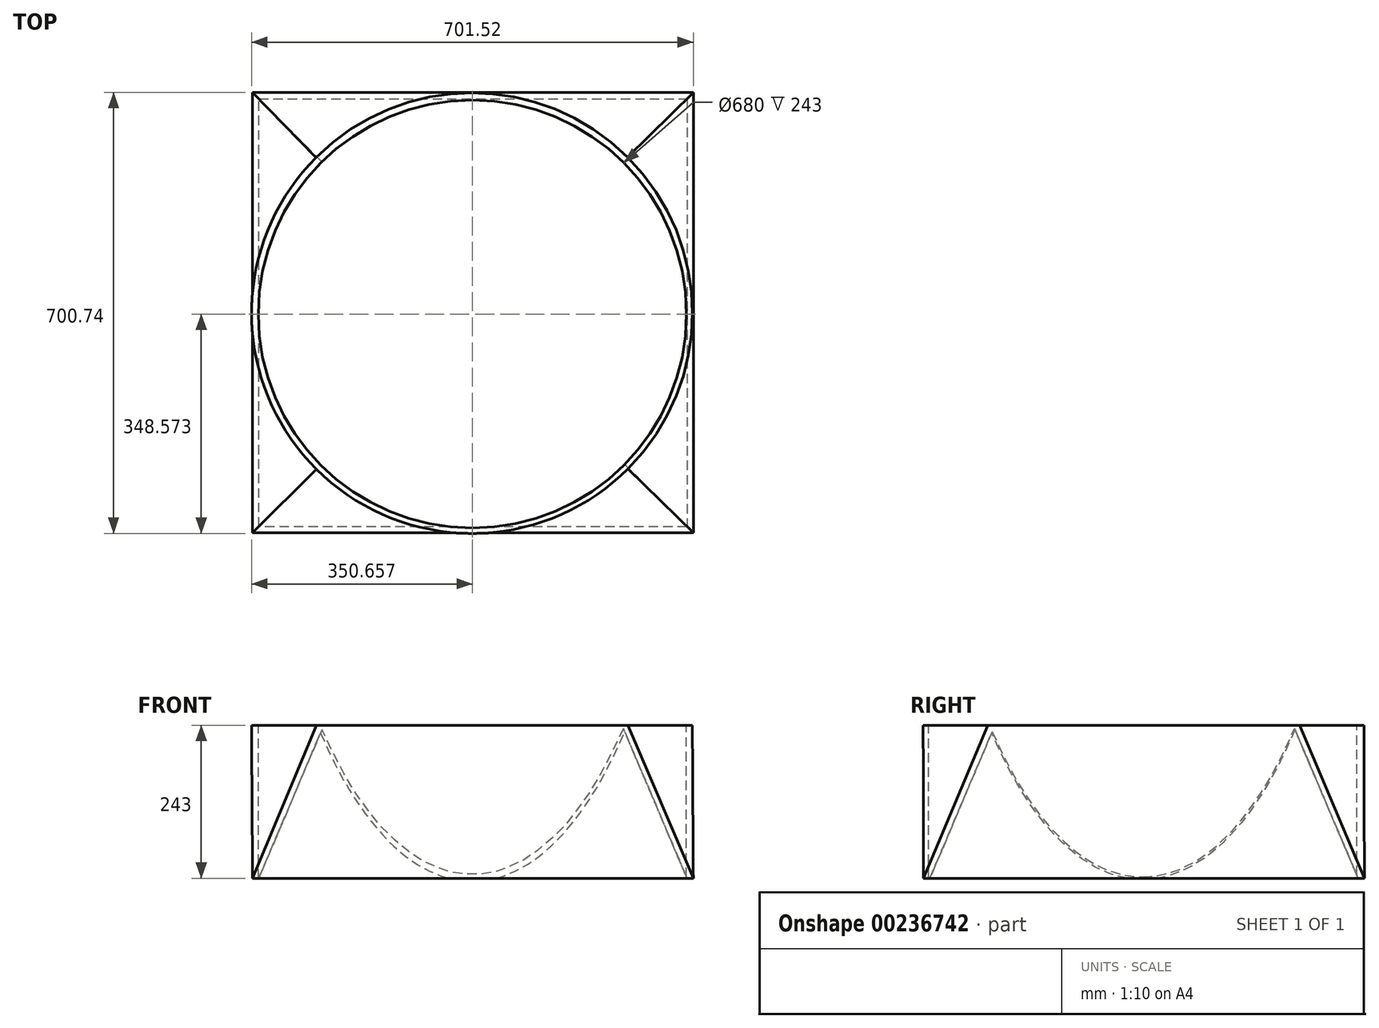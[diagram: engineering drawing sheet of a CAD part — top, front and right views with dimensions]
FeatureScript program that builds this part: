
annotation { "Feature Type Name" : "Feature", "Feature Type Description" : "" }
export const myFeature = defineFeature(function(context is Context, id is Id, definition is map)
    precondition{}
    {
        {
            var Q0;
            Q0=qCreatedBy(makeId("Top.planeOp"),FACE);
            var sketch = newSketch(context, id + "F0", { "sketchPlane" : qUnion([Q0])});
            skLineSegment(sketch, "E0.bottom", {"start": v(0, 0) * mm, "end": v(700, 0) * mm});
            skLineSegment(sketch, "E0.top", {"start": v(0, 700) * mm, "end": v(700, 700) * mm});
            skLineSegment(sketch, "E0.left", {"start": v(0, 0) * mm, "end": v(0, 700) * mm});
            skLineSegment(sketch, "E0.right", {"start": v(700, 0) * mm, "end": v(700, 700) * mm});
            skSolve(sketch);
        }
        {
            var Q0;
            Q0=makeQuery(id+"F0.imprint","IMPRINT",FACE,{"disambiguationData":[TD([[makeQuery(id+"F0.imprint","IMPRINT",EDGE,{"derivedFrom":sQuery(id+"F0.wireOp",EDGE,"E0.bottom")}),1.0]])]});
            cPlane(context, id + "F1", {"entities" : qUnion([Q0]), "cplaneType" : CPlaneType.OFFSET, "offset" : 243 * mm, "width" : 150 * mm, "height" : 150 * mm});
        }
        {
            var Q0;
            Q0=qCreatedBy(id+"F1.planeOp",FACE);
            var sketch = newSketch(context, id + "F2", { "sketchPlane" : qUnion([Q0])});
            skCircle(sketch, "E1", {"center": v(348.48, 349.26) * mm, "radius": 350 * mm});
            skLineSegment(sketch, "E2", {"start": v(0, 0) * mm, "end": v(696.95, 698.51) * mm, "construction": true});
            skLineSegment(sketch, "E3", {"start": v(0, 698.34) * mm, "end": v(698.47, 0) * mm, "construction": true});
            skSolve(sketch);
        }
        {
            var Q0;
            Q0=makeQuery(id+"F2.imprint","IMPRINT",FACE,{"disambiguationData":[TD([[makeQuery(id+"F2.imprint","IMPRINT",EDGE,{"derivedFrom":sQuery(id+"F2.wireOp",EDGE,"E1")}),1.0]])]});
            var Q1;
            Q1=makeQuery(id+"F0.imprint","IMPRINT",FACE,{"disambiguationData":[TD([[makeQuery(id+"F0.imprint","IMPRINT",EDGE,{"derivedFrom":sQuery(id+"F0.wireOp",EDGE,"E0.bottom")}),1.0]])]});
            loft(context, id + "F3", {"sheetProfilesArray" : [{ "sheetProfileEntities" : qUnion([Q0]) }, { "sheetProfileEntities" : qUnion([Q1]) }]});
        }
        {
            var Q0;
            Q0=makeQuery(id+"F3.opLoft","CAP_FACE",FACE,{"disambiguationData":[OSD([makeQuery(id+"F2.imprint","IMPRINT",FACE,{"disambiguationData":[TD([[makeQuery(id+"F2.imprint","IMPRINT",EDGE,{"derivedFrom":sQuery(id+"F2.wireOp",EDGE,"E1")}),1.0]])]})])],"isStart":true});
            var sketch = newSketch(context, id + "F4", { "sketchPlane" : qUnion([Q0])});
            skCircle(sketch, "E4", {"center": v(349.14, 347.83) * mm, "radius": 340 * mm});
            skSolve(sketch);
        }
        {
            var Q0;
            Q0=makeQuery(id+"F4.imprint","IMPRINT",FACE,{"disambiguationData":[TD([[makeQuery(id+"F4.imprint","IMPRINT",EDGE,{"derivedFrom":sQuery(id+"F4.wireOp",EDGE,"E4")}),1.0]])]});
            extrude(context, id + "F5", {"entities" : qUnion([Q0]), "operationType" : NewBodyOperationType.REMOVE, "endBound" : BoundingType.THROUGH_ALL, "oppositeDirection" : true, "depth" : 25 * mm, "offsetDistance" : 25 * mm});
        }
        {
            var Q0;
            Q0=makeQuery(id+"F3.opLoft","CAP_FACE",FACE,{"disambiguationData":[OSD([makeQuery(id+"F0.imprint","IMPRINT",FACE,{"disambiguationData":[TD([[makeQuery(id+"F0.imprint","IMPRINT",EDGE,{"derivedFrom":sQuery(id+"F0.wireOp",EDGE,"E0.bottom")}),1.0]])]})])],"isStart":true});
            var sketch = newSketch(context, id + "F6", { "sketchPlane" : qUnion([Q0])});
            skLineSegment(sketch, "E5.bottom", {"start": v(10, -10) * mm, "end": v(690, -10) * mm});
            skLineSegment(sketch, "E5.top", {"start": v(10, -690) * mm, "end": v(690, -690) * mm});
            skLineSegment(sketch, "E5.left", {"start": v(10, -10) * mm, "end": v(10, -690) * mm});
            skLineSegment(sketch, "E5.right", {"start": v(690, -10) * mm, "end": v(690, -690) * mm});
            skSolve(sketch);
        }
        {
            var Q0;
            Q0 = qSketchRegion(id + "F6", true);
            extrude(context, id + "F7", {"entities" : qUnion([Q0]), "operationType" : NewBodyOperationType.REMOVE, "oppositeDirection" : true, "depth" : 243 * mm, "offsetDistance" : 25 * mm, "hasDraft" : true, "draftAngle" : 23 * degree, "draftPullDirection" : true});
        }
    });
